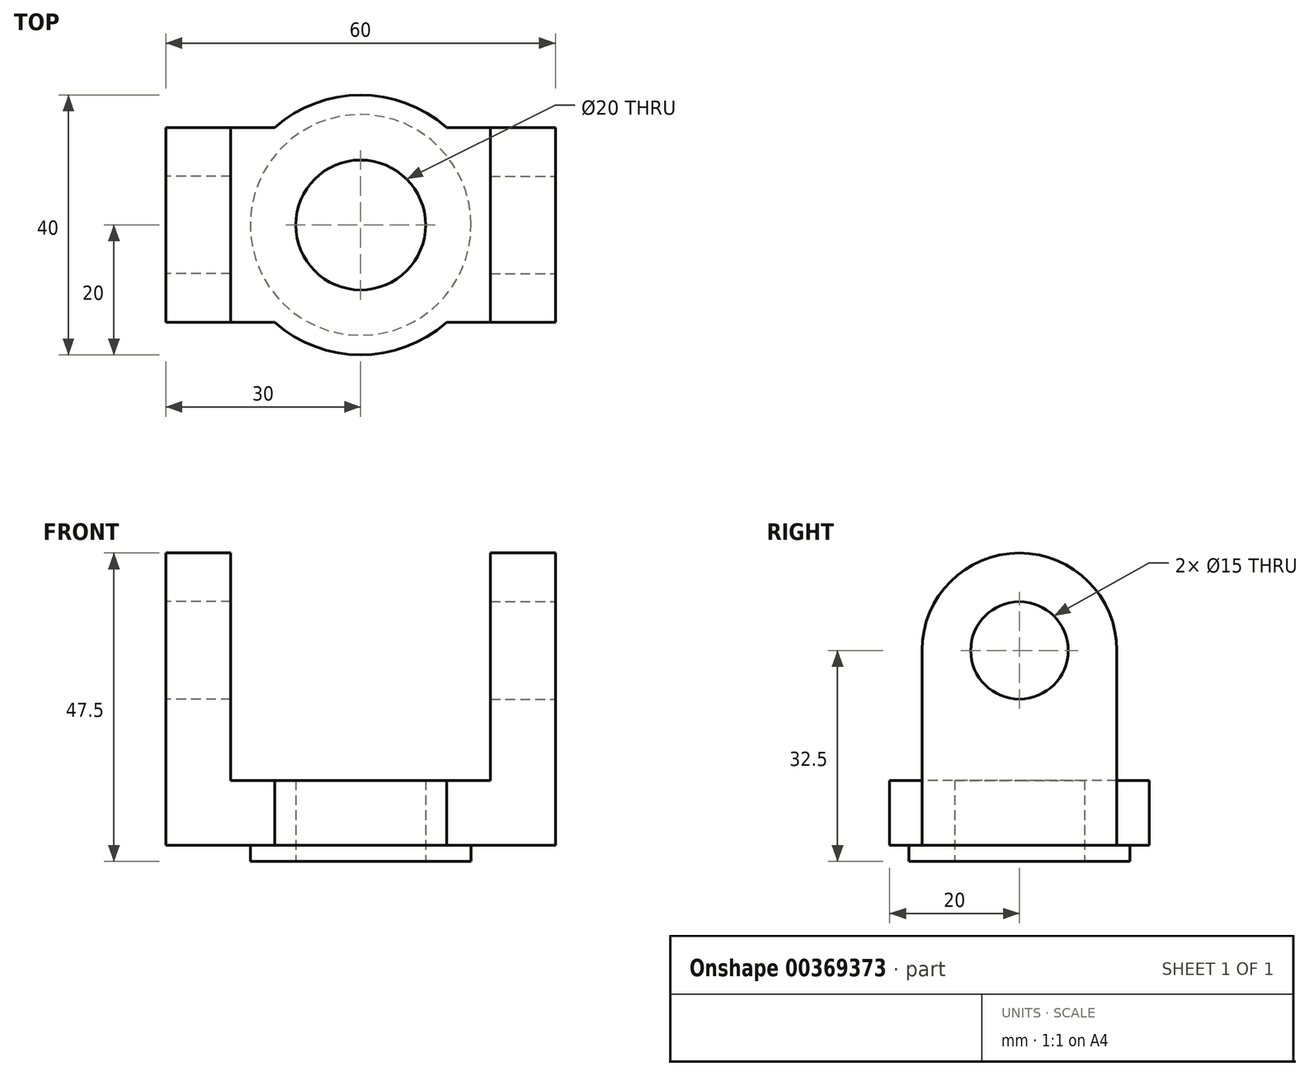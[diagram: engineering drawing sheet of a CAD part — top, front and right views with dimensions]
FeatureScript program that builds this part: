
annotation { "Feature Type Name" : "Feature", "Feature Type Description" : "" }
export const myFeature = defineFeature(function(context is Context, id is Id, definition is map)
    precondition{}
    {
        {
            var Q0;
            Q0=qCreatedBy(makeId("Top.planeOp"),FACE);
            var sketch = newSketch(context, id + "F0", { "sketchPlane" : qUnion([Q0])});
            skLineSegment(sketch, "E0", {"start": v(0, 0) * mm, "end": v(-30, 0) * mm});
            skLineSegment(sketch, "E1", {"start": v(-30, 0) * mm, "end": v(0, 0) * mm});
            skLineSegment(sketch, "E2", {"start": v(0, 0) * mm, "end": v(30, 0) * mm});
            skLineSegment(sketch, "E3", {"start": v(-30, 0) * mm, "end": v(-30, -30) * mm});
            skLineSegment(sketch, "E4", {"start": v(-30, -30) * mm, "end": v(30, -30) * mm});
            skLineSegment(sketch, "E5", {"start": v(30, -30) * mm, "end": v(30, 0) * mm});
            skLineSegment(sketch, "E6", {"start": v(-30, 0) * mm, "end": v(30, -30) * mm, "construction": true});
            skLineSegment(sketch, "E7", {"start": v(30, 0) * mm, "end": v(-30, -30) * mm, "construction": true});
            skCircle(sketch, "E8", {"center": v(0, -15) * mm, "radius": 20 * mm});
            skCircle(sketch, "E9", {"center": v(0, -15) * mm, "radius": 10 * mm});
            skSolve(sketch);
        }
        {
            var Q0;
            Q0 = qSketchRegion(id + "F0", true);
            extrude(context, id + "F1", {"entities" : qUnion([Q0]), "depth" : 10 * mm});
        }
        {
            var Q0;
            Q0=makeQuery(id+"F1.opExtrude","SWEPT_FACE",FACE,{"disambiguationData":[OSD([sQuery(id+"F0.wireOp",EDGE,"E5")])]});
            var sketch = newSketch(context, id + "F2", { "sketchPlane" : qUnion([Q0])});
            skLineSegment(sketch, "E10", {"start": v(-30, 10) * mm, "end": v(-30, 30) * mm});
            skLineSegment(sketch, "E11", {"start": v(-30, 30) * mm, "end": v(0, 30) * mm});
            skLineSegment(sketch, "E12", {"start": v(0, 30) * mm, "end": v(0, 10) * mm});
            skLineSegment(sketch, "E13", {"start": v(-30, 10) * mm, "end": v(0, 10) * mm});
            skArc(sketch, "E14", {"start": v(0, 30) * mm, "mid": v(-15, 45) * mm, "end": v(-30, 30) * mm});
            skCircle(sketch, "E15", {"center": v(-15, 30) * mm, "radius": 7.5 * mm});
            skSolve(sketch);
        }
        {
            var Q0;
            Q0 = qSketchRegion(id + "F2", true);
            extrude(context, id + "F3", {"entities" : qUnion([Q0]), "operationType" : NewBodyOperationType.ADD, "oppositeDirection" : true, "depth" : 10 * mm});
        }
        {
            var Q0;
            Q0=makeQuery(id+"F1.opExtrude","SWEPT_FACE",FACE,{"disambiguationData":[OSD([sQuery(id+"F0.wireOp",EDGE,"E3")])]});
            var sketch = newSketch(context, id + "F4", { "sketchPlane" : qUnion([Q0])});
            skLineSegment(sketch, "E16", {"start": v(0, 10) * mm, "end": v(30, 10) * mm});
            skLineSegment(sketch, "E17", {"start": v(30, 10) * mm, "end": v(30, 30) * mm});
            skLineSegment(sketch, "E18", {"start": v(30, 30) * mm, "end": v(0, 30) * mm});
            skLineSegment(sketch, "E19", {"start": v(0, 30) * mm, "end": v(0, 10) * mm});
            skArc(sketch, "E20", {"start": v(30, 30) * mm, "mid": v(15, 45) * mm, "end": v(0, 30) * mm});
            skCircle(sketch, "E21", {"center": v(15, 30) * mm, "radius": 7.5 * mm});
            skSolve(sketch);
        }
        {
            var Q0;
            Q0 = qSketchRegion(id + "F4", true);
            extrude(context, id + "F5", {"entities" : qUnion([Q0]), "operationType" : NewBodyOperationType.ADD, "oppositeDirection" : true, "depth" : 10 * mm});
        }
        {
            var Q0;
            Q0=makeQuery(id+"F1.opExtrude","CAP_FACE",FACE,{"disambiguationData":[OSD([sQuery(id+"F0.wireOp",EDGE,"E1"),sQuery(id+"F0.wireOp",EDGE,"E2"),sQuery(id+"F0.wireOp",EDGE,"E3"),sQuery(id+"F0.wireOp",EDGE,"E4"),sQuery(id+"F0.wireOp",EDGE,"E5"),sQuery(id+"F0.wireOp",EDGE,"E8"),sQuery(id+"F0.wireOp",EDGE,"E9")])],"isStart":true});
            var sketch = newSketch(context, id + "F6", { "sketchPlane" : qUnion([Q0])});
            skCircle(sketch, "E22", {"center": v(0, 15) * mm, "radius": 17 * mm});
            skCircle(sketch, "E23", {"center": v(0, 15) * mm, "radius": 10 * mm});
            skSolve(sketch);
        }
        {
            var Q0;
            Q0 = qSketchRegion(id + "F6", true);
            extrude(context, id + "F7", {"entities" : qUnion([Q0]), "operationType" : NewBodyOperationType.ADD, "depth" : 2.5 * mm});
        }
    });
